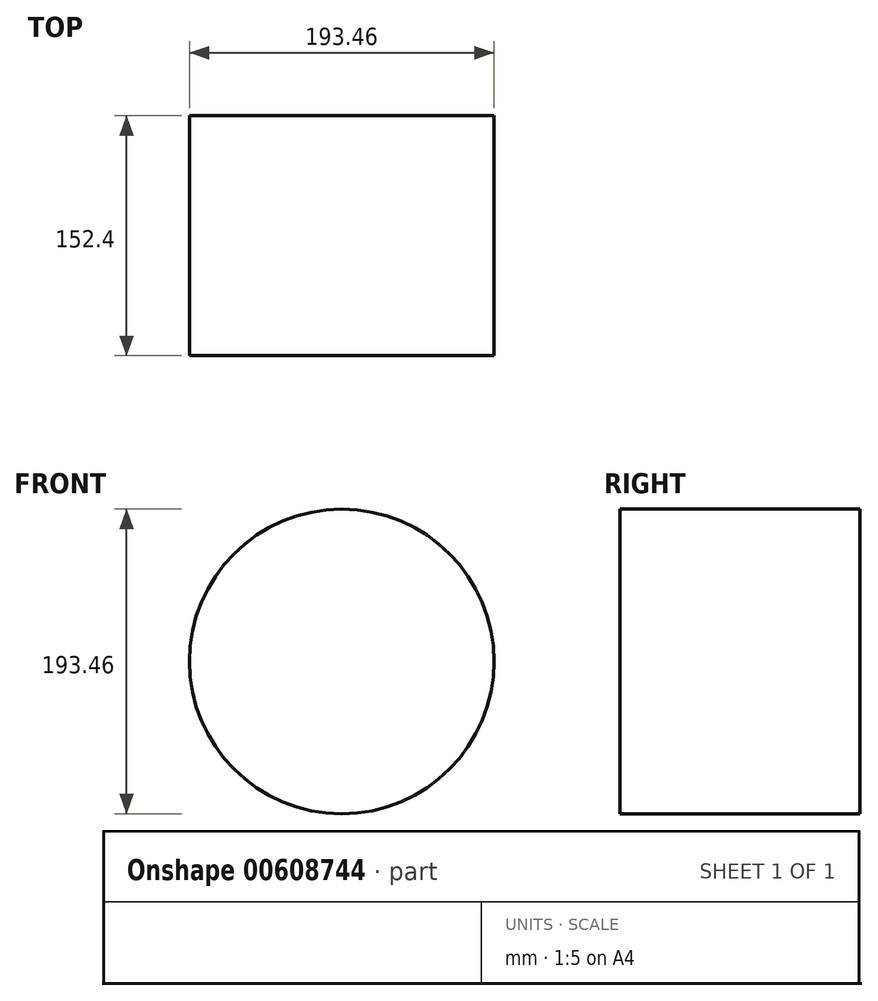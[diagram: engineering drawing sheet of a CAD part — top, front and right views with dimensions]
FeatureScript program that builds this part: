
annotation { "Feature Type Name" : "Feature", "Feature Type Description" : "" }
export const myFeature = defineFeature(function(context is Context, id is Id, definition is map)
    precondition{}
    {
        {
            var Q0;
            Q0=qCreatedBy(makeId("Front.planeOp"),FACE);
            var sketch = newSketch(context, id + "F0", { "sketchPlane" : qUnion([Q0])});
            skCircle(sketch, "E0", {"center": v(68.5, -26.23) * mm, "radius": 96.73 * mm});
            skSolve(sketch);
        }
        {
            var Q0;
            Q0=makeQuery(id+"F0.imprint","IMPRINT",FACE,{"disambiguationData":[TD([[makeQuery(id+"F0.imprint","IMPRINT",EDGE,{"derivedFrom":sQuery(id+"F0.wireOp",EDGE,"E0")}),1.0]])]});
            extrude(context, id + "F1", {"entities" : qUnion([Q0]), "depth" : 152.4 * mm, "offsetDistance" : 25.4 * mm});
        }
    });
